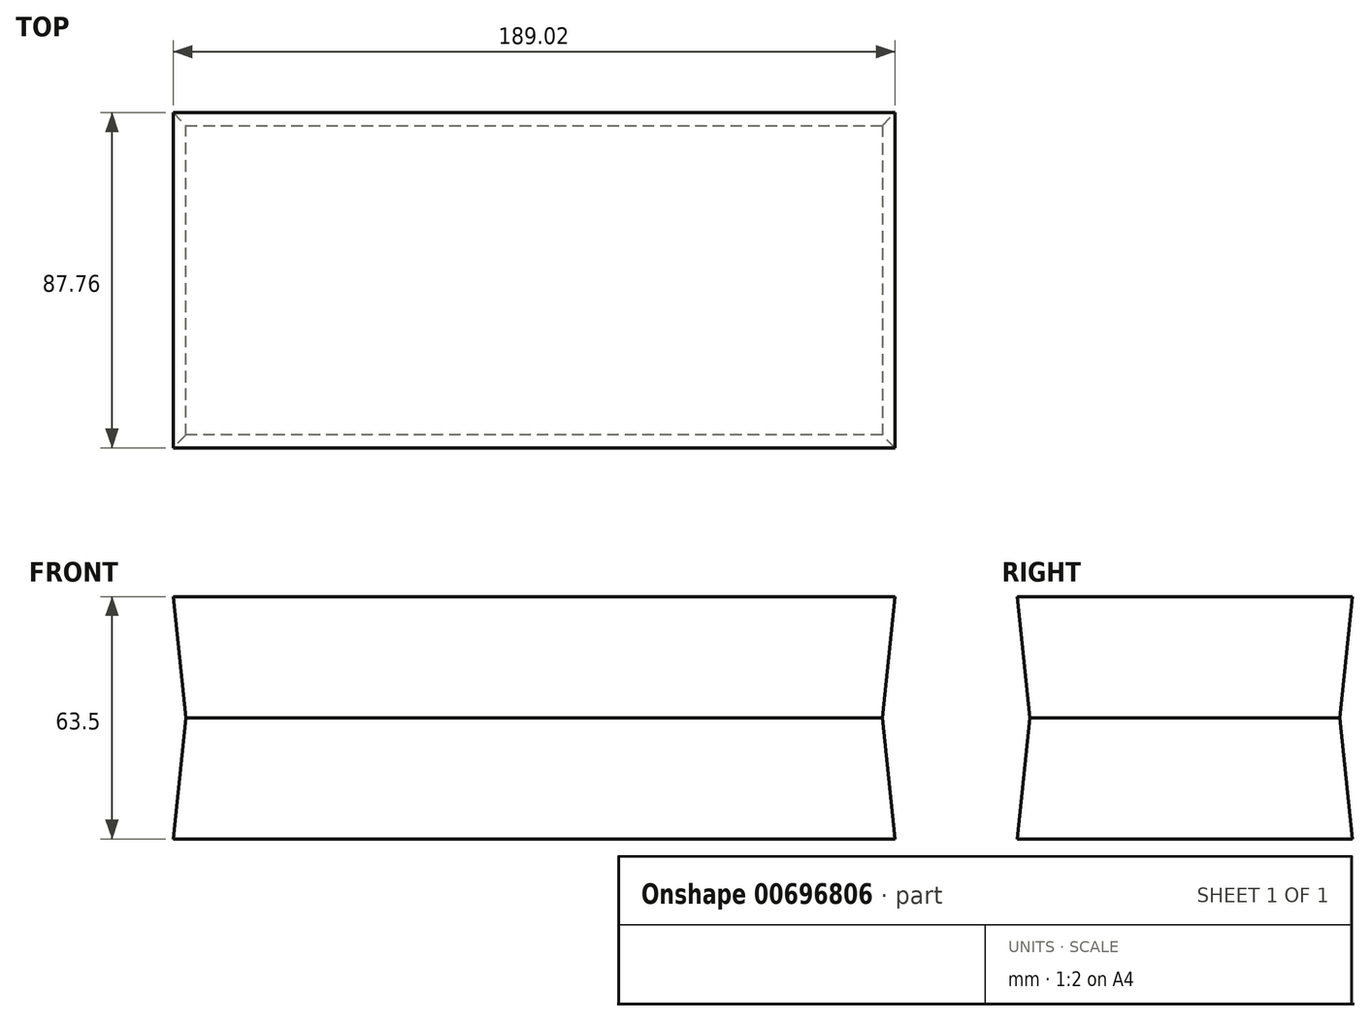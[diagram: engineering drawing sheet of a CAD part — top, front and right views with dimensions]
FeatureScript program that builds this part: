
annotation { "Feature Type Name" : "Feature", "Feature Type Description" : "" }
export const myFeature = defineFeature(function(context is Context, id is Id, definition is map)
    precondition{}
    {
        {
            var Q0;
            Q0=qCreatedBy(makeId("Top.planeOp"),FACE);
            var sketch = newSketch(context, id + "F0", { "sketchPlane" : qUnion([Q0])});
            skLineSegment(sketch, "E0.bottom", {"start": v(91.17, 40.54) * mm, "end": v(-91.17, 40.54) * mm});
            skLineSegment(sketch, "E0.top", {"start": v(91.17, -40.54) * mm, "end": v(-91.17, -40.54) * mm});
            skLineSegment(sketch, "E0.left", {"start": v(91.17, 40.54) * mm, "end": v(91.17, -40.54) * mm});
            skLineSegment(sketch, "E0.right", {"start": v(-91.17, 40.54) * mm, "end": v(-91.17, -40.54) * mm});
            skPoint(sketch, "E0.middle", {"position": v(0, 0) * mm});
            skSolve(sketch);
        }
        {
            var Q0;
            Q0 = qSketchRegion(id + "F0", true);
            extrude(context, id + "F1", {"entities" : qUnion([Q0]), "endBound" : BoundingType.SYMMETRIC, "depth" : 63.5 * mm, "offsetDistance" : 25.4 * mm, "hasDraft" : true, "draftAngle" : 6 * degree});
        }
    });
